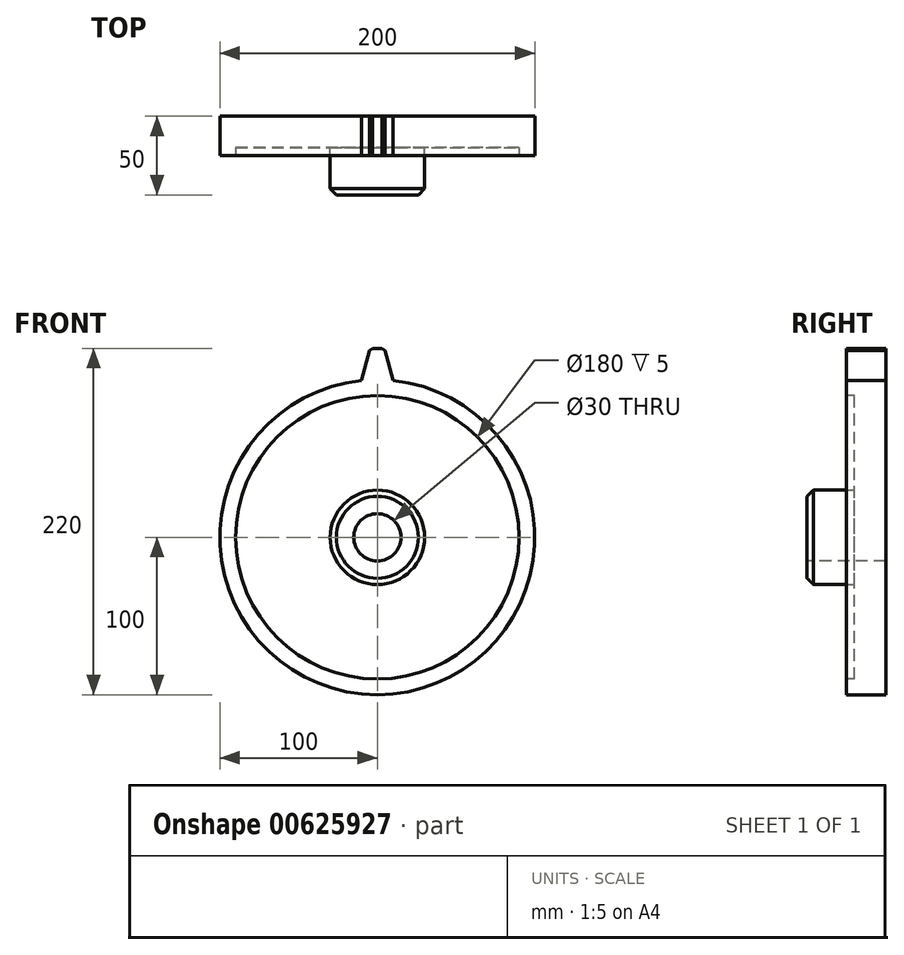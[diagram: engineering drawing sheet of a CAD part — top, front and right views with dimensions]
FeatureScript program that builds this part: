
annotation { "Feature Type Name" : "Feature", "Feature Type Description" : "" }
export const myFeature = defineFeature(function(context is Context, id is Id, definition is map)
    precondition{}
    {
        {
            var Q0;
            Q0=qCreatedBy(makeId("Front.planeOp"),FACE);
            var sketch = newSketch(context, id + "F0", { "sketchPlane" : qUnion([Q0])});
            skCircle(sketch, "E0", {"center": v(0, 0) * mm, "radius": 100 * mm});
            skSolve(sketch);
        }
        {
            var Q0;
            Q0=makeQuery(id+"F0.imprint","IMPRINT",FACE,{"disambiguationData":[TD([[makeQuery(id+"F0.imprint","IMPRINT",EDGE,{"derivedFrom":sQuery(id+"F0.wireOp",EDGE,"E0")}),1.0]])]});
            extrude(context, id + "F1", {"entities" : qUnion([Q0]), "depth" : 25 * mm, "offsetDistance" : 25 * mm});
        }
        {
            var Q0;
            Q0=makeQuery(id+"F1.opExtrude","CAP_FACE",FACE,{"disambiguationData":[OSD([sQuery(id+"F0.wireOp",EDGE,"E0")])],"isStart":true});
            var sketch = newSketch(context, id + "F2", { "sketchPlane" : qUnion([Q0])});
            skCircle(sketch, "E1", {"center": v(0, 0) * mm, "radius": 120 * mm, "construction": true});
            skPoint(sketch, "E2", {"position": v(0, 120) * mm});
            skLineSegment(sketch, "E3", {"start": v(-4.5, 120) * mm, "end": v(4.5, 120) * mm});
            skLineSegment(sketch, "E4", {"start": v(-4.5, 120) * mm, "end": v(-10, 99.5) * mm});
            skLineSegment(sketch, "E5", {"start": v(4.5, 120) * mm, "end": v(10, 99.5) * mm});
            skLineSegment(sketch, "E6", {"start": v(10, 99.5) * mm, "end": v(-10, 99.5) * mm});
            skSolve(sketch);
        }
        {
            var Q0;
            Q0=makeQuery(id+"F2.imprint","IMPRINT",FACE,{"disambiguationData":[TD([[makeQuery(id+"F2.imprint","IMPRINT",EDGE,{"derivedFrom":sQuery(id+"F2.wireOp",EDGE,"E3")}),-1.0]])]});
            var Q1;
            {var subQ0=sQuery(id+"F2.wireOp",EDGE,"E6");Q1=makeQuery(id+"F2.imprint","IMPRINT",FACE,{"disambiguationData":[TD([[makeQuery(id+"F2.imprint","IMPRINT",EDGE,{"derivedFrom":subQ0}),-1.0]])]});}
            extrude(context, id + "F3", {"entities" : qUnion([Q0, Q1]), "operationType" : NewBodyOperationType.ADD, "oppositeDirection" : true, "depth" : 25 * mm, "offsetDistance" : 25 * mm});
        }
        {
            var Q0;
            Q0=makeQuery(id+"F3.opExtrude","SWEPT_EDGE",EDGE,{"disambiguationData":[OSD([sQuery(id+"F2.wireOp",EDGE,"E3"),sQuery(id+"F2.wireOp",EDGE,"E5")])]});
            var Q1;
            Q1=makeQuery(id+"F3.opExtrude","SWEPT_EDGE",EDGE,{"disambiguationData":[OSD([sQuery(id+"F2.wireOp",EDGE,"E3"),sQuery(id+"F2.wireOp",EDGE,"E4")])]});
            chamfer(context, id + "F4", {"entities" : qUnion([Q0, Q1]), "width" : 2 * mm, "tangentPropagation" : true});
        }
        {
            var Q0;
            Q0=makeQuery(id+"F3.opExtrude","SWEPT_EDGE",EDGE,{"disambiguationData":[OSD([sQuery(id+"F0.wireOp",EDGE,"E0"),sQuery(id+"F2.wireOp",EDGE,"E5"),sQuery(id+"F2.wireOp",EDGE,"E6")])]});
            var Q1;
            Q1=makeQuery(id+"F3.opExtrude","SWEPT_EDGE",EDGE,{"disambiguationData":[OSD([sQuery(id+"F0.wireOp",EDGE,"E0"),sQuery(id+"F2.wireOp",EDGE,"E4"),sQuery(id+"F2.wireOp",EDGE,"E6")])]});
            fillet(context, id + "F5", {"entities" : qUnion([Q0, Q1]), "radius" : 5 * mm, "tangentPropagation" : true, "allowEdgeOverflow" : false});
        }
        {
            var Q0;
            {var subQ0=sQuery(id+"F2.wireOp",EDGE,"E6");var subQ1=sQuery(id+"F2.wireOp",EDGE,"E5");var subQ2=sQuery(id+"F2.wireOp",EDGE,"E4");var subQ3=sQuery(id+"F2.wireOp",EDGE,"E3");Q0=makeQuery(id+"FheeZmaJsr2lDKG_1.19.F3.boolean.opBoolean","MERGE",FACE,{"derivedFrom":[makeQuery(id+"FheeZmaJsr2lDKG_1.18.F3.boolean.opBoolean","MERGE",FACE,{"derivedFrom":[makeQuery(id+"FheeZmaJsr2lDKG_1.17.F3.boolean.opBoolean","MERGE",FACE,{"derivedFrom":[makeQuery(id+"FheeZmaJsr2lDKG_1.16.F3.boolean.opBoolean","MERGE",FACE,{"derivedFrom":[makeQuery(id+"FheeZmaJsr2lDKG_1.15.F3.boolean.opBoolean","MERGE",FACE,{"derivedFrom":[makeQuery(id+"FheeZmaJsr2lDKG_1.14.F3.boolean.opBoolean","MERGE",FACE,{"derivedFrom":[makeQuery(id+"FheeZmaJsr2lDKG_1.13.F3.boolean.opBoolean","MERGE",FACE,{"derivedFrom":[makeQuery(id+"FheeZmaJsr2lDKG_1.12.F3.boolean.opBoolean","MERGE",FACE,{"derivedFrom":[makeQuery(id+"FheeZmaJsr2lDKG_1.11.F3.boolean.opBoolean","MERGE",FACE,{"derivedFrom":[makeQuery(id+"FheeZmaJsr2lDKG_1.10.F3.boolean.opBoolean","MERGE",FACE,{"derivedFrom":[makeQuery(id+"FheeZmaJsr2lDKG_1.9.F3.boolean.opBoolean","MERGE",FACE,{"derivedFrom":[makeQuery(id+"FheeZmaJsr2lDKG_1.8.F3.boolean.opBoolean","MERGE",FACE,{"derivedFrom":[makeQuery(id+"FheeZmaJsr2lDKG_1.7.F3.boolean.opBoolean","MERGE",FACE,{"derivedFrom":[makeQuery(id+"FheeZmaJsr2lDKG_1.6.F3.boolean.opBoolean","MERGE",FACE,{"derivedFrom":[makeQuery(id+"FheeZmaJsr2lDKG_1.5.F3.boolean.opBoolean","MERGE",FACE,{"derivedFrom":[makeQuery(id+"FheeZmaJsr2lDKG_1.4.F3.boolean.opBoolean","MERGE",FACE,{"derivedFrom":[makeQuery(id+"FheeZmaJsr2lDKG_1.3.F3.boolean.opBoolean","MERGE",FACE,{"derivedFrom":[makeQuery(id+"FheeZmaJsr2lDKG_1.2.F3.boolean.opBoolean","MERGE",FACE,{"derivedFrom":[makeQuery(id+"FheeZmaJsr2lDKG_1.1.F3.boolean.opBoolean","MERGE",FACE,{"derivedFrom":[makeQuery(id+"F3.boolean.opBoolean","MERGE",FACE,{"derivedFrom":[makeQuery(id+"F1.opExtrude","CAP_FACE",FACE,{"disambiguationData":[OSD([sQuery(id+"F0.wireOp",EDGE,"E0")])],"isStart":false}),makeQuery(id+"F3.opExtrude","CAP_FACE",FACE,{"disambiguationData":[OSD([subQ3,subQ2,subQ1,subQ0])],"isStart":false})]}),makeQuery(id+"FheeZmaJsr2lDKG_1.1.F3.opExtrude","CAP_FACE",FACE,{"disambiguationData":[OSD([subQ3,subQ2,subQ1,subQ0])],"isStart":false})]}),makeQuery(id+"FheeZmaJsr2lDKG_1.2.F3.opExtrude","CAP_FACE",FACE,{"disambiguationData":[OSD([subQ3,subQ2,subQ1,subQ0])],"isStart":false})]}),makeQuery(id+"FheeZmaJsr2lDKG_1.3.F3.opExtrude","CAP_FACE",FACE,{"disambiguationData":[OSD([subQ3,subQ2,subQ1,subQ0])],"isStart":false})]}),makeQuery(id+"FheeZmaJsr2lDKG_1.4.F3.opExtrude","CAP_FACE",FACE,{"disambiguationData":[OSD([subQ3,subQ2,subQ1,subQ0])],"isStart":false})]}),makeQuery(id+"FheeZmaJsr2lDKG_1.5.F3.opExtrude","CAP_FACE",FACE,{"disambiguationData":[OSD([subQ3,subQ2,subQ1,subQ0])],"isStart":false})]}),makeQuery(id+"FheeZmaJsr2lDKG_1.6.F3.opExtrude","CAP_FACE",FACE,{"disambiguationData":[OSD([subQ3,subQ2,subQ1,subQ0])],"isStart":false})]}),makeQuery(id+"FheeZmaJsr2lDKG_1.7.F3.opExtrude","CAP_FACE",FACE,{"disambiguationData":[OSD([subQ3,subQ2,subQ1,subQ0])],"isStart":false})]}),makeQuery(id+"FheeZmaJsr2lDKG_1.8.F3.opExtrude","CAP_FACE",FACE,{"disambiguationData":[OSD([subQ3,subQ2,subQ1,subQ0])],"isStart":false})]}),makeQuery(id+"FheeZmaJsr2lDKG_1.9.F3.opExtrude","CAP_FACE",FACE,{"disambiguationData":[OSD([subQ3,subQ2,subQ1,subQ0])],"isStart":false})]}),makeQuery(id+"FheeZmaJsr2lDKG_1.10.F3.opExtrude","CAP_FACE",FACE,{"disambiguationData":[OSD([subQ3,subQ2,subQ1,subQ0])],"isStart":false})]}),makeQuery(id+"FheeZmaJsr2lDKG_1.11.F3.opExtrude","CAP_FACE",FACE,{"disambiguationData":[OSD([subQ3,subQ2,subQ1,subQ0])],"isStart":false})]}),makeQuery(id+"FheeZmaJsr2lDKG_1.12.F3.opExtrude","CAP_FACE",FACE,{"disambiguationData":[OSD([subQ3,subQ2,subQ1,subQ0])],"isStart":false})]}),makeQuery(id+"FheeZmaJsr2lDKG_1.13.F3.opExtrude","CAP_FACE",FACE,{"disambiguationData":[OSD([subQ3,subQ2,subQ1,subQ0])],"isStart":false})]}),makeQuery(id+"FheeZmaJsr2lDKG_1.14.F3.opExtrude","CAP_FACE",FACE,{"disambiguationData":[OSD([subQ3,subQ2,subQ1,subQ0])],"isStart":false})]}),makeQuery(id+"FheeZmaJsr2lDKG_1.15.F3.opExtrude","CAP_FACE",FACE,{"disambiguationData":[OSD([subQ3,subQ2,subQ1,subQ0])],"isStart":false})]}),makeQuery(id+"FheeZmaJsr2lDKG_1.16.F3.opExtrude","CAP_FACE",FACE,{"disambiguationData":[OSD([subQ3,subQ2,subQ1,subQ0])],"isStart":false})]}),makeQuery(id+"FheeZmaJsr2lDKG_1.17.F3.opExtrude","CAP_FACE",FACE,{"disambiguationData":[OSD([subQ3,subQ2,subQ1,subQ0])],"isStart":false})]}),makeQuery(id+"FheeZmaJsr2lDKG_1.18.F3.opExtrude","CAP_FACE",FACE,{"disambiguationData":[OSD([subQ3,subQ2,subQ1,subQ0])],"isStart":false})]}),makeQuery(id+"FheeZmaJsr2lDKG_1.19.F3.opExtrude","CAP_FACE",FACE,{"disambiguationData":[OSD([subQ3,subQ2,subQ1,subQ0])],"isStart":false})]});}
            var sketch = newSketch(context, id + "F6", { "sketchPlane" : qUnion([Q0])});
            skCircle(sketch, "E7", {"center": v(0, 0) * mm, "radius": 90 * mm});
            skSolve(sketch);
        }
        {
            var Q0;
            Q0=makeQuery(id+"F6.imprint","IMPRINT",FACE,{"disambiguationData":[TD([[makeQuery(id+"F6.imprint","IMPRINT",EDGE,{"derivedFrom":sQuery(id+"F6.wireOp",EDGE,"E7")}),1.0]])]});
            extrude(context, id + "F7", {"entities" : qUnion([Q0]), "operationType" : NewBodyOperationType.REMOVE, "oppositeDirection" : true, "depth" : 5 * mm, "offsetDistance" : 25 * mm});
        }
        {
            var Q0;
            Q0=makeQuery(id+"F7.boolean.opBoolean","COPY",FACE,{"derivedFrom":makeQuery(id+"F7.opExtrude","CAP_FACE",FACE,{"disambiguationData":[OSD([sQuery(id+"F6.wireOp",EDGE,"E7")])],"isStart":false})});
            var sketch = newSketch(context, id + "F8", { "sketchPlane" : qUnion([Q0])});
            skCircle(sketch, "E8", {"center": v(0, 0) * mm, "radius": 30 * mm});
            skSolve(sketch);
        }
        {
            var Q0;
            Q0=makeQuery(id+"F8.imprint","IMPRINT",FACE,{"disambiguationData":[TD([[makeQuery(id+"F8.imprint","IMPRINT",EDGE,{"derivedFrom":sQuery(id+"F8.wireOp",EDGE,"E8")}),1.0]])]});
            extrude(context, id + "F9", {"entities" : qUnion([Q0]), "operationType" : NewBodyOperationType.ADD, "depth" : 30 * mm, "offsetDistance" : 25 * mm});
        }
        {
            var Q0;
            Q0=makeQuery(id+"F9.opExtrude","CAP_FACE",FACE,{"disambiguationData":[OSD([sQuery(id+"F8.wireOp",EDGE,"E8")])],"isStart":false});
            var sketch = newSketch(context, id + "F10", { "sketchPlane" : qUnion([Q0])});
            skCircle(sketch, "E9", {"center": v(0, 0) * mm, "radius": 15 * mm});
            skSolve(sketch);
        }
        {
            var Q0;
            Q0=makeQuery(id+"F10.imprint","IMPRINT",FACE,{"disambiguationData":[TD([[makeQuery(id+"F10.imprint","IMPRINT",EDGE,{"derivedFrom":sQuery(id+"F10.wireOp",EDGE,"E9")}),1.0]])]});
            extrude(context, id + "F11", {"entities" : qUnion([Q0]), "operationType" : NewBodyOperationType.REMOVE, "endBound" : BoundingType.THROUGH_ALL, "oppositeDirection" : true, "depth" : 25 * mm, "offsetDistance" : 25 * mm});
        }
        {
            var Q0;
            Q0=makeQuery(id+"F11.boolean.opBoolean","COPY",EDGE,{"derivedFrom":makeQuery(id+"F11.opExtrude","CAP_EDGE",EDGE,{"disambiguationData":[OSD([sQuery(id+"F10.wireOp",EDGE,"E9")])],"isStart":true})});
            var Q1;
            Q1=makeQuery(id+"F9.opExtrude","CAP_EDGE",EDGE,{"disambiguationData":[OSD([sQuery(id+"F8.wireOp",EDGE,"E8")])],"isStart":false});
            chamfer(context, id + "F12", {"entities" : qUnion([Q0, Q1]), "width" : 4 * mm, "tangentPropagation" : true});
        }
    });
